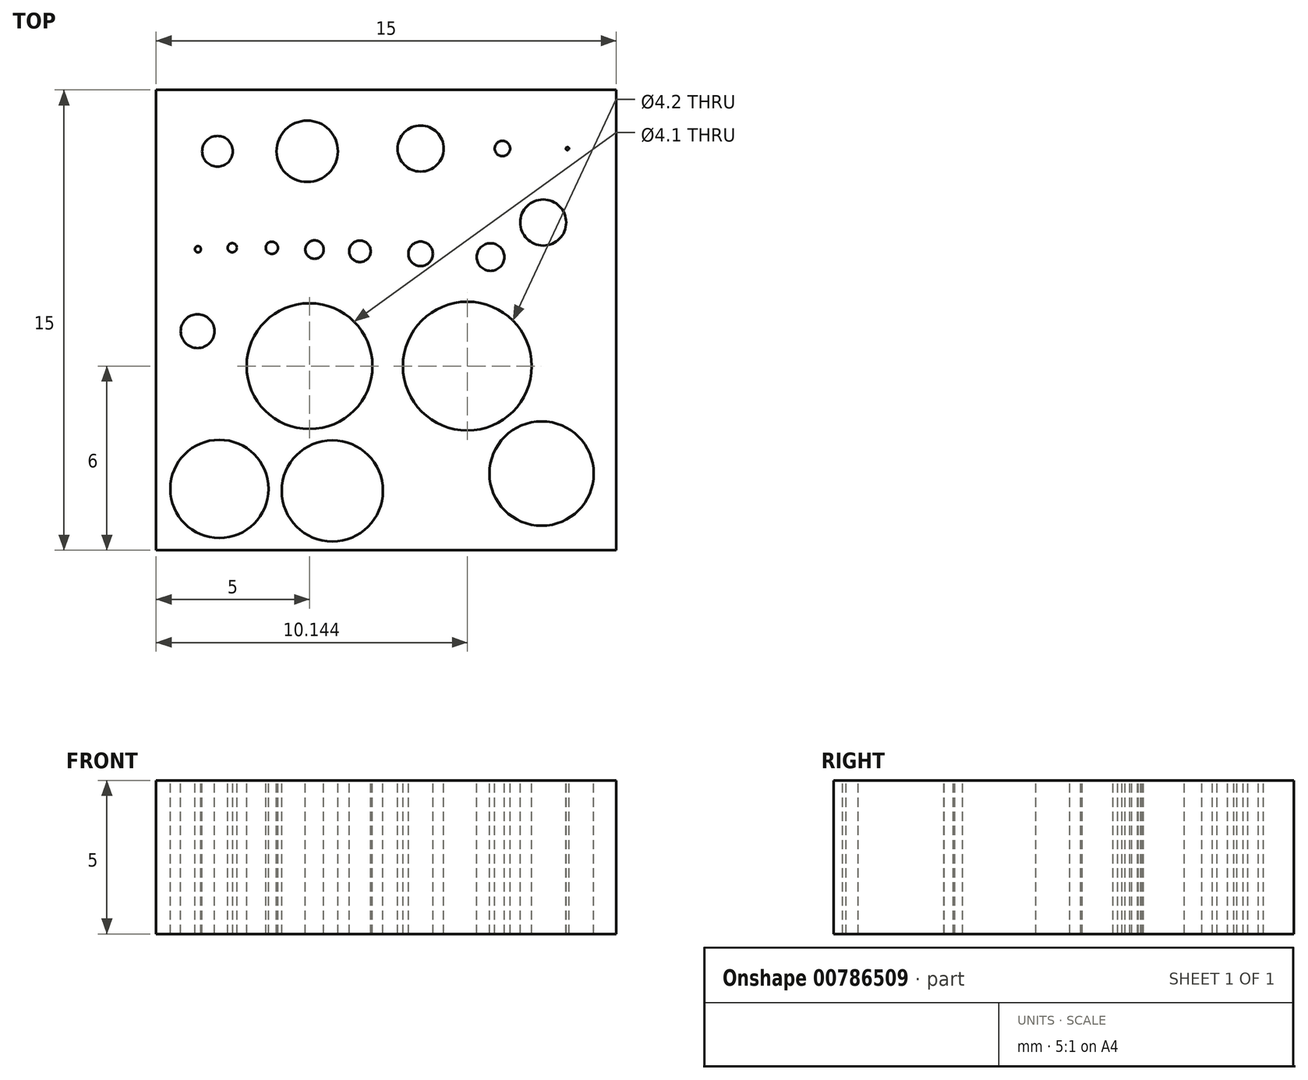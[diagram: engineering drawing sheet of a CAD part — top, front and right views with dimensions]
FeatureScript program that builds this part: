
annotation { "Feature Type Name" : "Feature", "Feature Type Description" : "" }
export const myFeature = defineFeature(function(context is Context, id is Id, definition is map)
    precondition{}
    {
        {
            var Q0;
            Q0=qCreatedBy(makeId("Top.planeOp"),FACE);
            var sketch = newSketch(context, id + "F0", { "sketchPlane" : qUnion([Q0])});
            skLineSegment(sketch, "E0.bottom", {"start": v(-7.5, 7.5) * mm, "end": v(7.5, 7.5) * mm});
            skLineSegment(sketch, "E0.top", {"start": v(-7.5, -7.5) * mm, "end": v(7.5, -7.5) * mm});
            skLineSegment(sketch, "E0.left", {"start": v(-7.5, 7.5) * mm, "end": v(-7.5, -7.5) * mm});
            skLineSegment(sketch, "E0.right", {"start": v(7.5, 7.5) * mm, "end": v(7.5, -7.5) * mm});
            skSolve(sketch);
        }
        {
            var Q0;
            Q0 = qSketchRegion(id + "F0", true);
            extrude(context, id + "F1", {"entities" : qUnion([Q0]), "depth" : 5 * mm, "offsetDistance" : 25 * mm});
        }
        {
            var Q0;
            Q0=makeQuery(id+"F1.opExtrude","CAP_FACE",FACE,{"disambiguationData":[OSD([sQuery(id+"F0.wireOp",EDGE,"E0.bottom"),sQuery(id+"F0.wireOp",EDGE,"E0.top"),sQuery(id+"F0.wireOp",EDGE,"E0.left"),sQuery(id+"F0.wireOp",EDGE,"E0.right")])],"isStart":false});
            var sketch = newSketch(context, id + "F2", { "sketchPlane" : qUnion([Q0])});
            skCircle(sketch, "E1", {"center": v(-5.5, 5.5) * mm, "radius": 0.5 * mm});
            skCircle(sketch, "E2", {"center": v(-2.57, 5.5) * mm, "radius": 1 * mm});
            skCircle(sketch, "E3", {"center": v(1.12, 5.59) * mm, "radius": 0.75 * mm});
            skCircle(sketch, "E4", {"center": v(3.79, 5.59) * mm, "radius": 0.25 * mm});
            skCircle(sketch, "E5", {"center": v(5.9, 5.59) * mm, "radius": 0.05 * mm});
            skCircle(sketch, "E6", {"center": v(-6.14, 2.3) * mm, "radius": 0.1 * mm});
            skCircle(sketch, "E7", {"center": v(-5.02, 2.36) * mm, "radius": 0.15 * mm});
            skCircle(sketch, "E8", {"center": v(-3.73, 2.35) * mm, "radius": 0.2 * mm});
            skCircle(sketch, "E9", {"center": v(-2.34, 2.3) * mm, "radius": 0.3 * mm});
            skCircle(sketch, "E10", {"center": v(-0.86, 2.24) * mm, "radius": 0.35 * mm});
            skCircle(sketch, "E11", {"center": v(1.12, 2.16) * mm, "radius": 0.4 * mm});
            skCircle(sketch, "E12", {"center": v(3.4, 2.05) * mm, "radius": 0.45 * mm});
            skCircle(sketch, "E13", {"center": v(-6.15, -0.36) * mm, "radius": 0.55 * mm});
            skCircle(sketch, "E14", {"center": v(-2.5, -1.5) * mm, "radius": 2.05 * mm});
            skCircle(sketch, "E15", {"center": v(2.64, -1.5) * mm, "radius": 2.1 * mm});
            skCircle(sketch, "E16", {"center": v(-5.44, -5.5) * mm, "radius": 1.6 * mm});
            skCircle(sketch, "E17", {"center": v(-1.76, -5.56) * mm, "radius": 1.65 * mm});
            skCircle(sketch, "E18", {"center": v(5.06, -5) * mm, "radius": 1.7 * mm});
            skCircle(sketch, "E19", {"center": v(5.12, 3.18) * mm, "radius": 0.75 * mm});
            skSolve(sketch);
        }
        {
            var Q0;
            Q0 = qSketchRegion(id + "F2", true);
            extrude(context, id + "F3", {"entities" : qUnion([Q0]), "operationType" : NewBodyOperationType.REMOVE, "oppositeDirection" : true, "depth" : 25 * mm, "offsetDistance" : 25 * mm});
        }
    });
